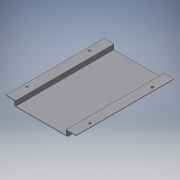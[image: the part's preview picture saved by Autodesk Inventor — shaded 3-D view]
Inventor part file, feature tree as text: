
AUTODESK INVENTOR PART (.ipt)
format: ipt  version: 2016 SP2 (Build 200236200, 236)  size: 125,952 bytes
history: native  units: mm
features: reference x6, extrude x3, sketch x2, projected_geometry x1
ambient origin geometry x8: Origin, YZ Plane, XZ Plane, XY Plane, X Axis, Y Axis, Z Axis, Center Point
bodies: Volumenkörper1 (feature_tree)
feature tree (12):
  extrude  "Extrusion1"  Depth=12.0mm
  extrude  "Extrusion3"  Depth=7.0mm TaperAngle=0.0deg
  extrude  "Extrusion4"  Depth=2.0mm
  reference  "Referenz1"
  sketch  "Skizze2"  dims[d2=0.6mm d3=0.0mm d4=12.0mm]
  sketch  "Skizze3"  dims[d5=12.0mm d8=7.0mm d9=0.0mm d10=2.0mm d11=2.0mm d12=7.0mm d13=0.0mm d14=25.75mm d15=25.0mm]
  projected_geometry  "Projizierte Kontur1"
  reference  "Referenz9"
  reference  "Referenz10"
  reference  "Referenz11"
  reference  "Referenz12"
  reference  "Referenz13"
